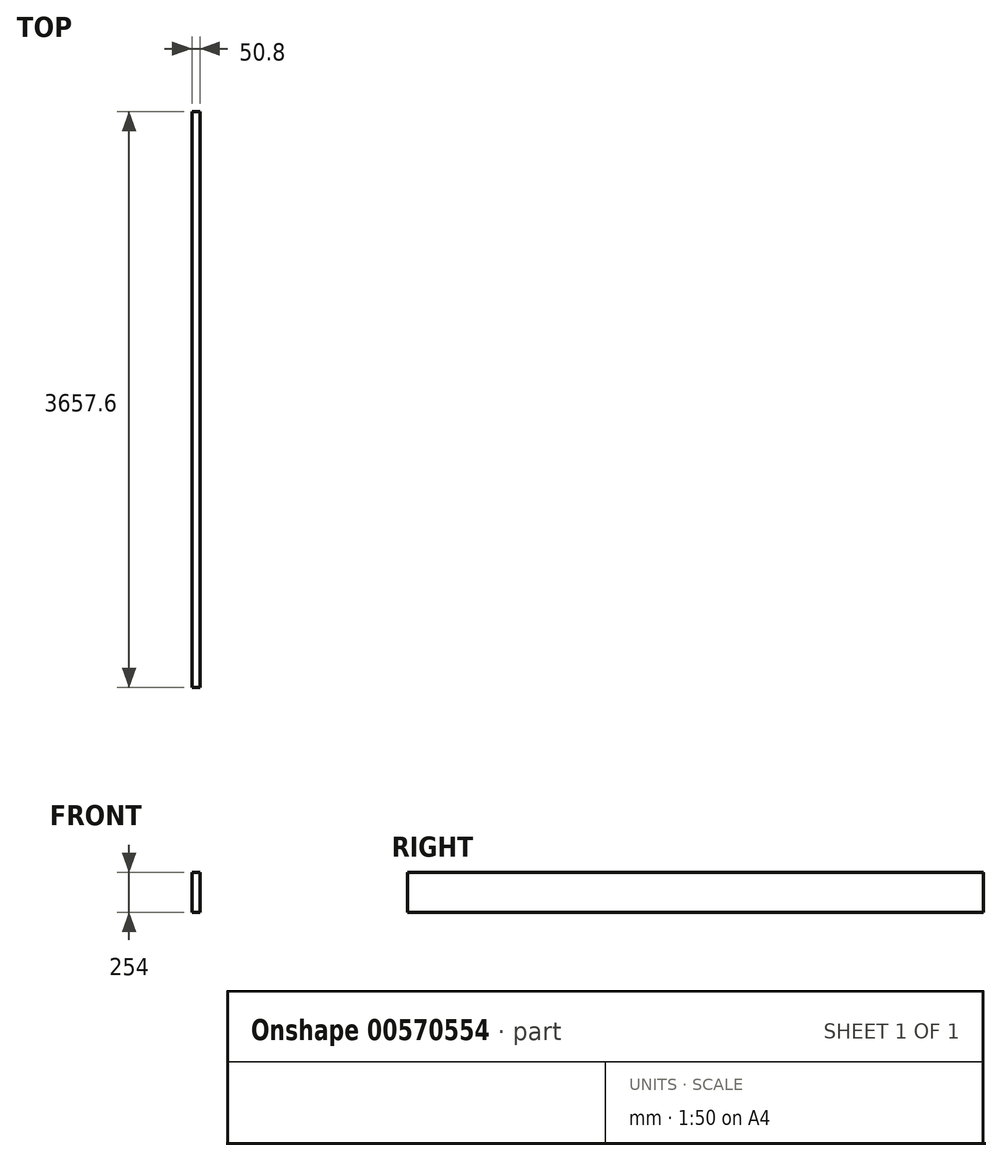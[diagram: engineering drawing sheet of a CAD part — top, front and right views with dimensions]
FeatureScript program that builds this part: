
annotation { "Feature Type Name" : "Feature", "Feature Type Description" : "" }
export const myFeature = defineFeature(function(context is Context, id is Id, definition is map)
    precondition{}
    {
        {
            var Q0;
            Q0=qCreatedBy(makeId("Front.planeOp"),FACE);
            var sketch = newSketch(context, id + "F0", { "sketchPlane" : qUnion([Q0])});
            skLineSegment(sketch, "E0.bottom", {"start": v(-25.4, -127) * mm, "end": v(25.4, -127) * mm});
            skLineSegment(sketch, "E0.top", {"start": v(-25.4, 127) * mm, "end": v(25.4, 127) * mm});
            skLineSegment(sketch, "E0.left", {"start": v(-25.4, -127) * mm, "end": v(-25.4, 127) * mm});
            skLineSegment(sketch, "E0.right", {"start": v(25.4, -127) * mm, "end": v(25.4, 127) * mm});
            skPoint(sketch, "E0.middle", {"position": v(0, 0) * mm});
            skSolve(sketch);
        }
        {
            var Q0;
            Q0 = qSketchRegion(id + "F0", true);
            extrude(context, id + "F1", {"entities" : qUnion([Q0]), "endBound" : BoundingType.SYMMETRIC, "depth" : 3657.6 * mm, "offsetDistance" : 25.4 * mm});
        }
    });
